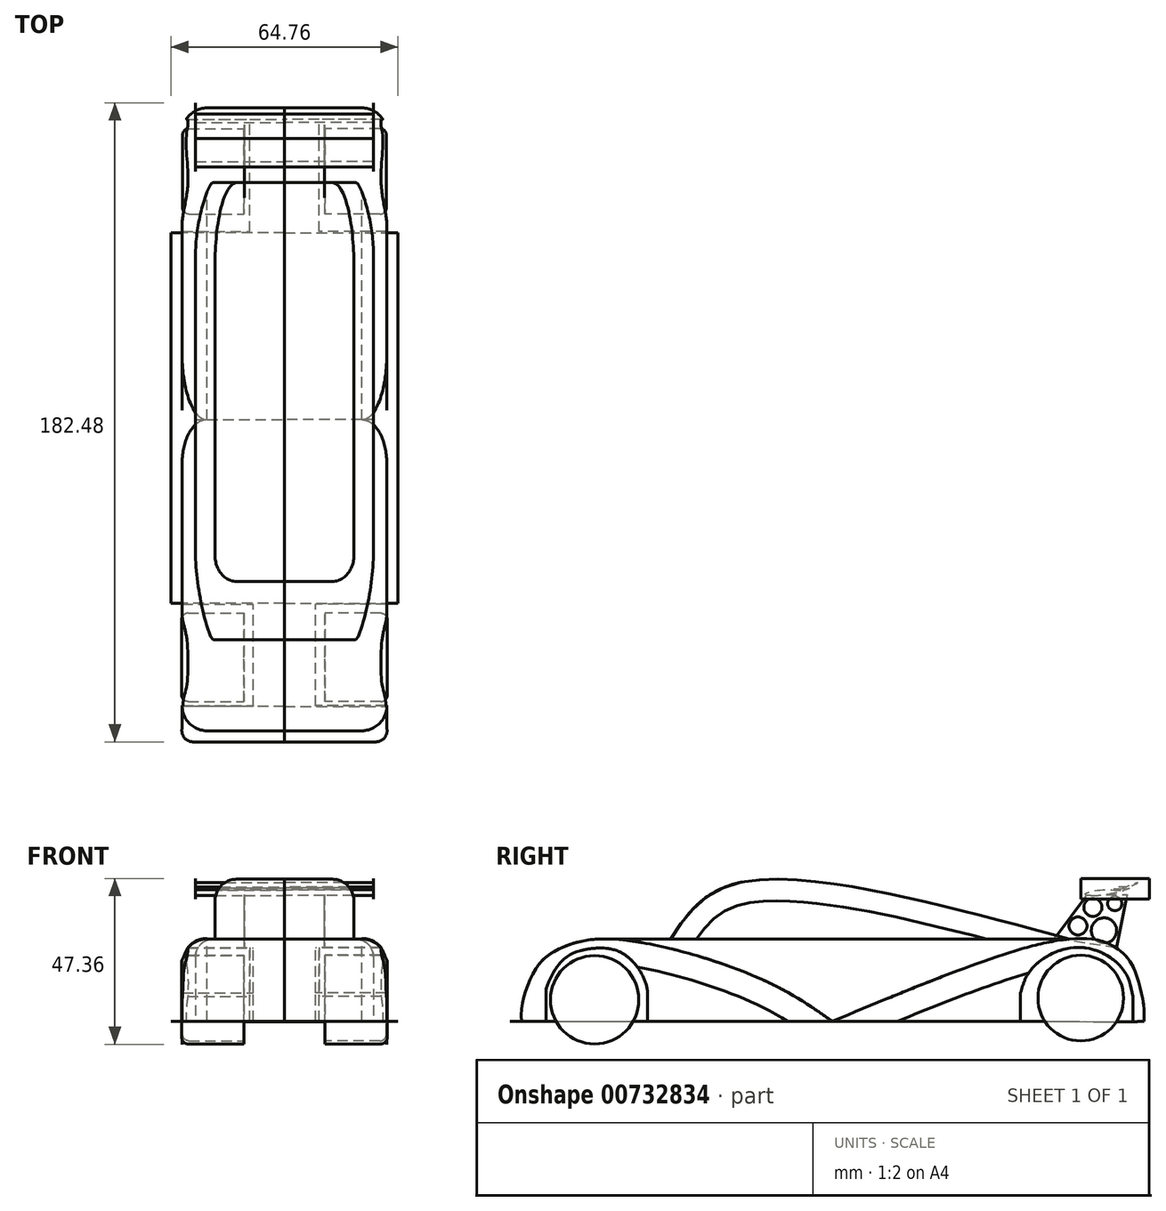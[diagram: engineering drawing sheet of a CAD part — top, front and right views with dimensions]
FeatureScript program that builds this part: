
annotation { "Feature Type Name" : "Feature", "Feature Type Description" : "" }
export const myFeature = defineFeature(function(context is Context, id is Id, definition is map)
    precondition{}
    {
        {
            var Q0;
            Q0=qCreatedBy(makeId("Right.planeOp"),FACE);
            var sketch = newSketch(context, id + "F0", { "sketchPlane" : qUnion([Q0])});
            skFitSpline(sketch, "E0", {"points": [v(-88.66, -15.18) * mm, v(-88.66, -11.24) * mm, v(-84.5, 0) * mm, v(-77.67, 5.62) * mm, v(-62.77, 8.3) * mm, v(-20.75, -2.93) * mm, v(0, -15.18) * mm], "startDerivative": vector(-4.51, 39.66) * mm, "endDerivative": vector(84.62, -59.82) * mm});
            skFitSpline(sketch, "E1", {"points": [v(88.95, -15.18) * mm, v(88.95, -11.48) * mm, v(86.02, 0) * mm, v(81.62, 5.37) * mm, v(75.51, 8.06) * mm, v(58.16, 6.6) * mm, v(0, -15.18) * mm], "startDerivative": vector(2.88, 35.72) * mm, "endDerivative": vector(-188.15, -78.3) * mm});
            skLineSegment(sketch, "E2", {"start": v(-62.77, 8.3) * mm, "end": v(67.7, 8.3) * mm});
            skLineSegment(sketch, "E3", {"start": v(-88.66, -15.18) * mm, "end": v(-81.67, -15.18) * mm});
            skLineSegment(sketch, "E4", {"start": v(-81.67, -15.18) * mm, "end": v(-81.67, -7.06) * mm});
            skLineSegment(sketch, "E5", {"start": v(-52.69, -15.18) * mm, "end": v(-52.69, -7.06) * mm});
            skFitSpline(sketch, "E6", {"points": [v(-81.67, -7.06) * mm, v(-81.67, -6.1) * mm, v(-78.81, 0) * mm, v(-74.25, 4.1) * mm, v(-67.65, 5.69) * mm, v(-60.87, 4.74) * mm, v(-55.41, 0) * mm, v(-52.69, -7.06) * mm], "startDerivative": vector(-2.4, 12.55) * mm, "endDerivative": vector(4.3, -46.7) * mm});
            skLineSegment(sketch, "E7", {"start": v(-52.69, -15.18) * mm, "end": v(53.74, -15.18) * mm});
            skLineSegment(sketch, "E8", {"start": v(53.74, -15.18) * mm, "end": v(53.74, -7.02) * mm});
            skLineSegment(sketch, "E9", {"start": v(88.95, -15.18) * mm, "end": v(85.8, -15.32) * mm});
            skLineSegment(sketch, "E10", {"start": v(85.8, -15.32) * mm, "end": v(85.8, -8.04) * mm});
            skFitSpline(sketch, "E11", {"points": [v(53.74, -7.02) * mm, v(57.12, 0) * mm, v(70.09, 5.95) * mm, v(82.75, 0) * mm, v(85.8, -8.04) * mm], "startDerivative": vector(9.74, 33.83) * mm, "endDerivative": vector(6.93, -37.5) * mm});
            skFitSpline(sketch, "E12", {"points": [v(-46.18, 8.3) * mm, v(-28.35, 23.94) * mm, v(67.7, 8.3) * mm], "startDerivative": vector(39.17, 58.98) * mm, "endDerivative": vector(173.44, -47) * mm});
            skLineSegment(sketch, "E13", {"start": v(-81.67, -15.18) * mm, "end": v(-52.69, -15.18) * mm});
            skLineSegment(sketch, "E14", {"start": v(53.74, -15.18) * mm, "end": v(85.8, -15.32) * mm});
            skFitSpline(sketch, "E15", {"points": [v(73.72, 20.69) * mm, v(80.14, 21.44) * mm, v(82.2, 21.94) * mm, v(84.89, 22.93) * mm], "startDerivative": vector(22.6, 0.68) * mm, "endDerivative": vector(2.9, 2.95) * mm});
            skFitSpline(sketch, "E16", {"points": [v(73.72, 20.69) * mm, v(72.18, 21.1) * mm, v(73.72, 21.9) * mm, v(79.05, 22.37) * mm, v(84.89, 22.93) * mm], "startDerivative": vector(-13.5, 0.17) * mm, "endDerivative": vector(16.17, 8.09) * mm});
            skFitSpline(sketch, "E17", {"points": [v(81.08, 22.6) * mm, v(82.5, 22.69) * mm, v(84.95, 23.3) * mm, v(87.28, 24.46) * mm, v(84.95, 23.57) * mm, v(82.46, 23.16) * mm, v(80.99, 23.14) * mm, v(80.3, 22.74) * mm, v(81.08, 22.6) * mm]});
            skSolve(sketch);
        }
        {
            var Q0;
            {var subQ0=sQuery(id+"F0.wireOp",EDGE,"E0");var subQ1=sQuery(id+"F0.wireOp",EDGE,"gzcjJU3f-WTno-5fRS-OjhX-LvgmPmwLUnIu");var subQ2=makeQuery(id+"F0.imprint","INTERSECT",VERTEX,{"derivedFrom":[subQ1,subQ0]});Q0=makeQuery(id+"F0.imprint","IMPRINT",FACE,{"disambiguationData":[TD([[makeQuery(id+"F0.imprint","IMPRINT",EDGE,{"disambiguationData":[TD([[subQ2,-1.0]])],"derivedFrom":subQ0}),-1.0]])]});}
            extrude(context, id + "F1", {"entities" : qUnion([Q0]), "depth" : 29.2 * mm, "offsetDistance" : 25.4 * mm});
        }
        {
            var Q0;
            {var subQ0=sQuery(id+"F0.wireOp",EDGE,"E1");var subQ1=sQuery(id+"F0.wireOp",EDGE,"gzcjJU3f-WTno-5fRS-OjhX-LvgmPmwLUnIu");var subQ2=makeQuery(id+"F0.imprint","INTERSECT",VERTEX,{"derivedFrom":[subQ1,subQ0]});Q0=makeQuery(id+"F0.imprint","IMPRINT",FACE,{"disambiguationData":[TD([[makeQuery(id+"F0.imprint","IMPRINT",EDGE,{"disambiguationData":[TD([[subQ2,-1.0]])],"derivedFrom":subQ0}),1.0]])]});}
            extrude(context, id + "F2", {"entities" : qUnion([Q0]), "depth" : 29.2 * mm, "offsetDistance" : 25.4 * mm});
        }
        {
            var Q0;
            {var subQ3=sQuery(id+"F0.wireOp",EDGE,"E2");Q0=makeQuery(id+"F0.imprint","IMPRINT",FACE,{"disambiguationData":[TD([[makeQuery(id+"F0.imprint","IMPRINT",EDGE,{"derivedFrom":subQ3}),-1.0]])]});}
            extrude(context, id + "F3", {"entities" : qUnion([Q0]), "depth" : 25.4 * mm, "offsetDistance" : 25.4 * mm});
        }
        {
            var Q0;
            Q0=makeQuery(id+"F2.opExtrude","CAP_EDGE",EDGE,{"disambiguationData":[OSD([sQuery(id+"F0.wireOp",EDGE,"E1")])],"isStart":false});
            fillet(context, id + "F4", {"entities" : qUnion([Q0]), "radius" : 7.11 * mm, "tangentPropagation" : true, "allowEdgeOverflow" : false});
        }
        {
            var Q0;
            Q0=makeQuery(id+"F3.opExtrude","CAP_EDGE",EDGE,{"disambiguationData":[OSD([sQuery(id+"F0.wireOp",EDGE,"E2")])],"isStart":false});
            fillet(context, id + "F5", {"entities" : qUnion([Q0]), "radius" : 5.08 * mm, "tangentPropagation" : true, "allowEdgeOverflow" : false});
        }
        {
            var Q0;
            Q0=makeQuery(id+"F1.opExtrude","CAP_EDGE",EDGE,{"disambiguationData":[OSD([sQuery(id+"F0.wireOp",EDGE,"E0")])],"isStart":false});
            fillet(context, id + "F6", {"entities" : qUnion([Q0]), "radius" : 7.11 * mm, "tangentPropagation" : true, "allowEdgeOverflow" : false});
        }
        {
            var Q0;
            Q0=makeQuery(id+"F2.opExtrude","SWEPT_FACE",FACE,{"disambiguationData":[OSD([sQuery(id+"F0.wireOp",EDGE,"E7")])]});
            cPlane(context, id + "F7", {"entities" : qUnion([Q0]), "cplaneType" : CPlaneType.OFFSET, "offset" : 0 * mm, "width" : 152.4 * mm, "height" : 152.4 * mm});
        }
        {
            var Q0;
            Q0=qCreatedBy(id+"F7.planeOp",FACE);
            var sketch = newSketch(context, id + "F8", { "sketchPlane" : qUnion([Q0])});
            skLineSegment(sketch, "E18.bottom", {"start": v(0, -53.44) * mm, "end": v(32.38, -53.44) * mm});
            skLineSegment(sketch, "E18.top", {"start": v(0, 52.41) * mm, "end": v(32.38, 52.41) * mm});
            skLineSegment(sketch, "E18.left", {"start": v(0, -53.44) * mm, "end": v(0, 52.41) * mm});
            skLineSegment(sketch, "E18.right", {"start": v(32.38, -53.44) * mm, "end": v(32.38, 52.41) * mm});
            skLineSegment(sketch, "E19.bottom", {"start": v(0, 81.83) * mm, "end": v(29.2, 81.83) * mm});
            skLineSegment(sketch, "E19.top", {"start": v(0, 88.74) * mm, "end": v(29.2, 88.74) * mm});
            skLineSegment(sketch, "E19.left", {"start": v(0, 81.83) * mm, "end": v(0, 88.74) * mm});
            skLineSegment(sketch, "E19.right", {"start": v(29.2, 81.83) * mm, "end": v(29.2, 88.74) * mm});
            skLineSegment(sketch, "E20.bottom", {"start": v(0, 88.74) * mm, "end": v(26.05, 88.74) * mm});
            skLineSegment(sketch, "E20.top", {"start": v(0, 91.98) * mm, "end": v(26.05, 91.98) * mm});
            skLineSegment(sketch, "E20.left", {"start": v(0, 88.74) * mm, "end": v(0, 91.98) * mm});
            skLineSegment(sketch, "E20.right", {"start": v(26.05, 88.74) * mm, "end": v(26.05, 91.98) * mm});
            skCircle(sketch, "E21", {"center": v(26.05, 88.74) * mm, "radius": 3.25 * mm});
            skSolve(sketch);
        }
        {
            var Q0;
            Q0 = qSketchRegion(id + "F8", true);
            extrude(context, id + "F9", {"entities" : qUnion([Q0]), "depth" : 0.03 * mm, "offsetDistance" : 25.4 * mm});
        }
        {
            var Q0;
            {var subQ0=sQuery(id+"F0.wireOp",EDGE,"E12");Q0=makeQuery(id+"F0.imprint","IMPRINT",FACE,{"disambiguationData":[TD([[makeQuery(id+"F0.imprint","IMPRINT",EDGE,{"derivedFrom":subQ0}),-1.0]])]});}
            extrude(context, id + "F10", {"entities" : qUnion([Q0]), "operationType" : NewBodyOperationType.ADD, "depth" : 19.8 * mm, "offsetDistance" : 25.4 * mm});
        }
        {
            var Q0;
            Q0=makeQuery(id+"F10.opExtrude","CAP_EDGE",EDGE,{"disambiguationData":[OSD([sQuery(id+"F0.wireOp",EDGE,"E12")])],"isStart":false});
            fillet(context, id + "F11", {"entities" : qUnion([Q0]), "radius" : 6.13 * mm, "tangentPropagation" : true, "allowEdgeOverflow" : false});
        }
        {
            var Q0;
            {var subQ4=sQuery(id+"F0.wireOp",EDGE,"E4");Q0=makeQuery(id+"F0.imprint","IMPRINT",FACE,{"disambiguationData":[TD([[makeQuery(id+"F0.imprint","IMPRINT",EDGE,{"derivedFrom":subQ4}),-1.0]])]});}
            extrude(context, id + "F12", {"entities" : qUnion([Q0]), "operationType" : NewBodyOperationType.ADD, "depth" : 8.64 * mm, "offsetDistance" : 25.4 * mm});
        }
        {
            var Q0;
            {var subQ0=sQuery(id+"F0.wireOp",EDGE,"gJ9o0Lnp-IIpX-0cl1-lVzv-iZYszRdgN0eT");var subQ1=sQuery(id+"F0.wireOp",EDGE,"E13");var subQ2=makeQuery(id+"F0.imprint","INTERSECT",VERTEX,{"disambiguationData":[OD(0.0)],"derivedFrom":[subQ1,subQ0]});Q0=makeQuery(id+"F0.imprint","IMPRINT",FACE,{"disambiguationData":[TD([[makeQuery(id+"F0.imprint","IMPRINT",EDGE,{"disambiguationData":[TD([[subQ2,-1.0]])],"derivedFrom":subQ1}),1.0]])]});}
            extrude(context, id + "F13", {"entities" : qUnion([Q0]), "operationType" : NewBodyOperationType.ADD, "depth" : 8.9 * mm, "offsetDistance" : 25.4 * mm});
        }
        {
            var Q0;
            {var subQ1=sQuery(id+"F0.wireOp",EDGE,"E8");Q0=makeQuery(id+"F0.imprint","IMPRINT",FACE,{"disambiguationData":[TD([[makeQuery(id+"F0.imprint","IMPRINT",EDGE,{"derivedFrom":subQ1}),-1.0]])]});}
            extrude(context, id + "F14", {"entities" : qUnion([Q0]), "operationType" : NewBodyOperationType.ADD, "depth" : 9.9 * mm, "offsetDistance" : 25.4 * mm});
        }
        {
            var Q0;
            Q0=makeQuery(id+"F13.opExtrude","CAP_FACE",FACE,{"disambiguationData":[OSD([sQuery(id+"F0.wireOp",EDGE,"E4"),sQuery(id+"F0.wireOp",EDGE,"E5"),sQuery(id+"F0.wireOp",EDGE,"E6"),sQuery(id+"F0.wireOp",EDGE,"E13")])],"isStart":false});
            cPlane(context, id + "F15", {"entities" : qUnion([Q0]), "cplaneType" : CPlaneType.OFFSET, "offset" : 2.54 * mm, "width" : 152.4 * mm, "height" : 152.4 * mm});
        }
        {
            var Q0;
            Q0=qCreatedBy(id+"F15.planeOp",FACE);
            var sketch = newSketch(context, id + "F16", { "sketchPlane" : qUnion([Q0])});
            skCircle(sketch, "E22", {"center": v(-67.4, -9.04) * mm, "radius": 11.62 * mm});
            skCircle(sketch, "E23", {"center": v(70.5, -8.76) * mm, "radius": 11.65 * mm});
            skLineSegment(sketch, "E24", {"start": v(63.47, 8.53) * mm, "end": v(72.84, 21.06) * mm});
            skLineSegment(sketch, "E25", {"start": v(72.84, 21.06) * mm, "end": v(84.19, 21.06) * mm});
            skLineSegment(sketch, "E26", {"start": v(84.19, 21.06) * mm, "end": v(81.15, 5.76) * mm});
            skLineSegment(sketch, "E27", {"start": v(81.15, 5.76) * mm, "end": v(63.47, 8.53) * mm});
            skCircle(sketch, "E28", {"center": v(74.39, 17.37) * mm, "radius": 2.58 * mm});
            skCircle(sketch, "E29", {"center": v(80.63, 18.45) * mm, "radius": 2.03 * mm});
            skCircle(sketch, "E30", {"center": v(77.55, 10.74) * mm, "radius": 3.61 * mm});
            skCircle(sketch, "E31", {"center": v(70.15, 12.05) * mm, "radius": 2.57 * mm});
            skSolve(sketch);
        }
        {
            var Q0;
            Q0=makeQuery(id+"F16.imprint","IMPRINT",FACE,{"disambiguationData":[TD([[makeQuery(id+"F16.imprint","IMPRINT",EDGE,{"derivedFrom":sQuery(id+"F16.wireOp",EDGE,"E24")}),-1.0]])]});
            extrude(context, id + "F17", {"entities" : qUnion([Q0]), "depth" : 0 * mm, "offsetDistance" : 25.4 * mm});
        }
        {
            var Q0;
            Q0=qCreatedBy(id+"F15.planeOp",FACE);
            cPlane(context, id + "F18", {"entities" : qUnion([Q0]), "cplaneType" : CPlaneType.OFFSET, "offset" : 0.13 * mm, "width" : 152.4 * mm, "height" : 152.4 * mm});
        }
        {
            var Q0;
            Q0=qCreatedBy(id+"F18.planeOp",FACE);
            var sketch = newSketch(context, id + "F19", { "sketchPlane" : qUnion([Q0])});
            skCircle(sketch, "E32", {"center": v(-67.84, -9.04) * mm, "radius": 12.62 * mm});
            skCircle(sketch, "E33", {"center": v(70.93, -8.55) * mm, "radius": 12.22 * mm});
            skSolve(sketch);
        }
        {
            var Q0;
            Q0=makeQuery(id+"F19.imprint","IMPRINT",FACE,{"disambiguationData":[TD([[makeQuery(id+"F19.imprint","IMPRINT",EDGE,{"derivedFrom":sQuery(id+"F19.wireOp",EDGE,"E32")}),1.0]])]});
            extrude(context, id + "F20", {"entities" : qUnion([Q0]), "depth" : 17.78 * mm, "offsetDistance" : 25.4 * mm});
        }
        {
            var Q0;
            Q0=makeQuery(id+"F19.imprint","IMPRINT",FACE,{"disambiguationData":[TD([[makeQuery(id+"F19.imprint","IMPRINT",EDGE,{"derivedFrom":sQuery(id+"F19.wireOp",EDGE,"E33")}),1.0]])]});
            extrude(context, id + "F21", {"entities" : qUnion([Q0]), "depth" : 17.53 * mm, "offsetDistance" : 25.4 * mm});
        }
        {
            var Q0;
            Q0=makeQuery(id+"F20.opExtrude","CAP_FACE",FACE,{"disambiguationData":[OSD([sQuery(id+"F19.wireOp",EDGE,"E32")])],"isStart":false});
            fillet(context, id + "F22", {"entities" : qUnion([Q0]), "radius" : 1.84 * mm, "tangentPropagation" : true, "allowEdgeOverflow" : false});
        }
        {
            var Q0;
            Q0=makeQuery(id+"F21.opExtrude","CAP_FACE",FACE,{"disambiguationData":[OSD([sQuery(id+"F19.wireOp",EDGE,"E33")])],"isStart":false});
            fillet(context, id + "F23", {"entities" : qUnion([Q0]), "radius" : 1.83 * mm, "tangentPropagation" : true, "allowEdgeOverflow" : false});
        }
        {
            var Q0;
            Q0=makeQuery(id+"F0.imprint","IMPRINT",FACE,{"disambiguationData":[TD([[makeQuery(id+"F0.imprint","IMPRINT",EDGE,{"derivedFrom":sQuery(id+"F0.wireOp",EDGE,"E15")}),1.0]])]});
            extrude(context, id + "F24", {"entities" : qUnion([Q0]), "operationType" : NewBodyOperationType.ADD, "depth" : 25.4 * mm, "offsetDistance" : 25.4 * mm});
        }
        {
            var Q0;
            Q0=makeQuery(id+"F24.opExtrude","CAP_FACE",FACE,{"disambiguationData":[OSD([sQuery(id+"F0.wireOp",EDGE,"E15"),sQuery(id+"F0.wireOp",EDGE,"E16")])],"isStart":false});
            cPlane(context, id + "F25", {"entities" : qUnion([Q0]), "cplaneType" : CPlaneType.OFFSET, "offset" : 0 * mm, "width" : 152.4 * mm, "height" : 152.4 * mm});
        }
        {
            var Q0;
            Q0=qCreatedBy(id+"F25.planeOp",FACE);
            var sketch = newSketch(context, id + "F26", { "sketchPlane" : qUnion([Q0])});
            skLineSegment(sketch, "E34.bottom", {"start": v(70.94, 25.6) * mm, "end": v(90.5, 25.6) * mm});
            skLineSegment(sketch, "E34.top", {"start": v(70.94, 19.78) * mm, "end": v(90.5, 19.78) * mm});
            skLineSegment(sketch, "E34.left", {"start": v(70.94, 25.6) * mm, "end": v(70.94, 19.78) * mm});
            skLineSegment(sketch, "E34.right", {"start": v(90.5, 25.6) * mm, "end": v(90.5, 19.78) * mm});
            skSolve(sketch);
        }
        {
            var Q0;
            Q0=makeQuery(id+"F26.imprint","IMPRINT",FACE,{"disambiguationData":[TD([[makeQuery(id+"F26.imprint","IMPRINT",EDGE,{"derivedFrom":sQuery(id+"F26.wireOp",EDGE,"E34.bottom")}),-1.0]])]});
            extrude(context, id + "F27", {"entities" : qUnion([Q0]), "operationType" : NewBodyOperationType.ADD, "depth" : 0.03 * mm, "offsetDistance" : 25.4 * mm});
        }
        {
            var Q0;
            Q0=makeQuery(id+"F0.imprint","IMPRINT",FACE,{"disambiguationData":[TD([[makeQuery(id+"F0.imprint","IMPRINT",EDGE,{"derivedFrom":sQuery(id+"F0.wireOp",EDGE,"E17")}),1.0]])]});
            extrude(context, id + "F28", {"entities" : qUnion([Q0]), "operationType" : NewBodyOperationType.ADD, "depth" : 25.4 * mm, "offsetDistance" : 25.4 * mm});
        }
        {
            var Q0;
            Q0=makeQuery(id+"F1.opExtrude","SWEPT_BODY",BODY,{"disambiguationData":[OSD([sQuery(id+"F0.wireOp",EDGE,"E0"),sQuery(id+"F0.wireOp",EDGE,"E3"),sQuery(id+"F0.wireOp",EDGE,"E4"),sQuery(id+"F0.wireOp",EDGE,"E5"),sQuery(id+"F0.wireOp",EDGE,"E6"),sQuery(id+"F0.wireOp",EDGE,"E7")])]});
            var Q1;
            Q1=makeQuery(id+"F2.opExtrude","SWEPT_BODY",BODY,{"disambiguationData":[OSD([sQuery(id+"F0.wireOp",EDGE,"E1"),sQuery(id+"F0.wireOp",EDGE,"E7"),sQuery(id+"F0.wireOp",EDGE,"E8"),sQuery(id+"F0.wireOp",EDGE,"E9"),sQuery(id+"F0.wireOp",EDGE,"E10"),sQuery(id+"F0.wireOp",EDGE,"E11")])]});
            var Q2;
            Q2=makeQuery(id+"F3.opExtrude","SWEPT_BODY",BODY,{"disambiguationData":[OSD([sQuery(id+"F0.wireOp",EDGE,"E0"),sQuery(id+"F0.wireOp",EDGE,"E1"),sQuery(id+"F0.wireOp",EDGE,"E2")])]});
            var Q3;
            Q3=makeQuery(id+"F9.opExtrude","SWEPT_BODY",BODY,{"disambiguationData":[OSD([sQuery(id+"F8.wireOp",EDGE,"E18.bottom"),sQuery(id+"F8.wireOp",EDGE,"E18.top"),sQuery(id+"F8.wireOp",EDGE,"E18.left"),sQuery(id+"F8.wireOp",EDGE,"E18.right")])]});
            var Q4;
            Q4=makeQuery(id+"F9.opExtrude","SWEPT_BODY",BODY,{"disambiguationData":[OSD([sQuery(id+"F8.wireOp",EDGE,"E19.bottom"),sQuery(id+"F8.wireOp",EDGE,"E19.left"),sQuery(id+"F8.wireOp",EDGE,"E19.right"),sQuery(id+"F8.wireOp",EDGE,"E20.top"),sQuery(id+"F8.wireOp",EDGE,"E20.left"),sQuery(id+"F8.wireOp",EDGE,"E21")])]});
            var Q5;
            Q5=makeQuery(id+"F17.opExtrude","SWEPT_BODY",BODY,{"disambiguationData":[OSD([sQuery(id+"F16.wireOp",EDGE,"E24"),sQuery(id+"F16.wireOp",EDGE,"E25"),sQuery(id+"F16.wireOp",EDGE,"E26"),sQuery(id+"F16.wireOp",EDGE,"E27"),sQuery(id+"F16.wireOp",EDGE,"E28"),sQuery(id+"F16.wireOp",EDGE,"E29"),sQuery(id+"F16.wireOp",EDGE,"E30"),sQuery(id+"F16.wireOp",EDGE,"E31")])]});
            var Q6;
            Q6=makeQuery(id+"F20.opExtrude","SWEPT_BODY",BODY,{"disambiguationData":[OSD([sQuery(id+"F19.wireOp",EDGE,"E32")])]});
            var Q7;
            Q7=makeQuery(id+"F21.opExtrude","SWEPT_BODY",BODY,{"disambiguationData":[OSD([sQuery(id+"F19.wireOp",EDGE,"E33")])]});
            var Q8;
            Q8=qCreatedBy(makeId("Right.planeOp"),FACE);
            mirror(context, id + "F29", {"entities" : qUnion([Q0, Q1, Q2, Q3, Q4, Q5, Q6, Q7]), "mirrorPlane" : qUnion([Q8])});
        }
    });
